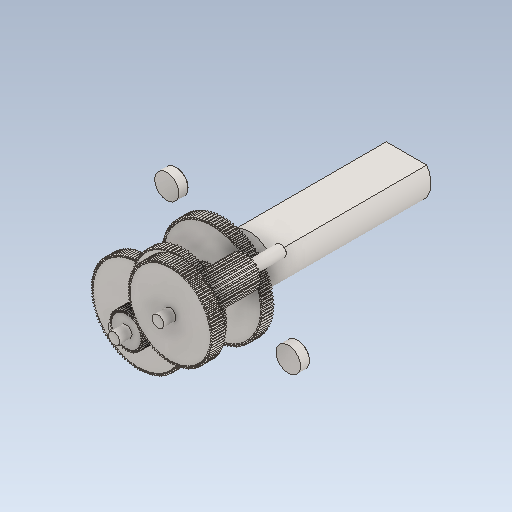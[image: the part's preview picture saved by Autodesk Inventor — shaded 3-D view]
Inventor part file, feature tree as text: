
AUTODESK INVENTOR PART (.ipt)
format: ipt  version: 2020 (Build 240168000, 168)  size: 2,567,680 bytes
history: mixed  units: in
note: dims shown in document units (in); Inventor stores cm internally (conversion verified against a paired STEP export)
features: other x3, fillet x2, imported_body x1
ambient origin geometry x8: Origin, YZ Plane, XZ Plane, XY Plane, X Axis, Y Axis, Z Axis, Center Point
bodies: Solid1 (imported_parasolid), Solid2 (imported_parasolid), Solid3 (imported_parasolid), Solid4 (imported_parasolid), Solid5 (imported_parasolid)
feature tree (6):
  other  "Boss-Extrude5"
  other  "Boss-Extrude7"
  other  "Boss-Extrude16"
  fillet  "Fillet2"  [1 undecoded]
  fillet  "Fillet3"  [1 undecoded]
  imported_body  NMx_Import_Brep_tag  [imported B-rep: ~2690 faces, bbox_mm=[11.101946, 10.166736, 17.9]]
note: 2 required parameter values undecoded (feature->parameter linkage not recoverable at this tier; creation-order binding heuristic only, values carry confidence <= 0.55)
